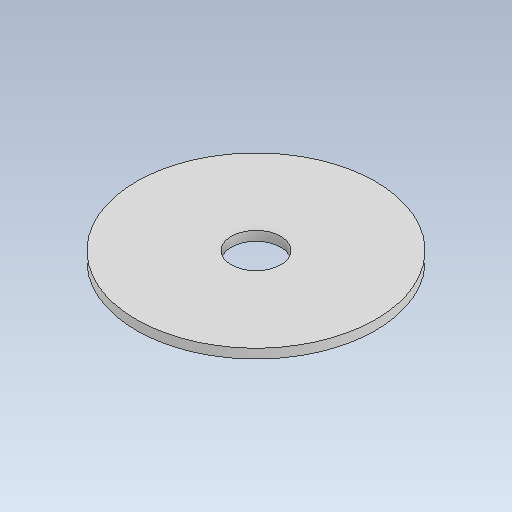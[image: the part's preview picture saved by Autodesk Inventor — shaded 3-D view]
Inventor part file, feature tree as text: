
AUTODESK INVENTOR PART (.ipt)
format: ipt  version: 2023 (Build 270158000, 158)  size: 88,576 bytes
history: native  units: in
note: dims shown in document units (in); Inventor stores cm internally (conversion verified against a paired STEP export)
features: extrude x1, sketch x1
ambient origin geometry x8: Origin, YZ Plane, XZ Plane, XY Plane, X Axis, Y Axis, Z Axis, Center Point
bodies: Solid1 (feature_tree)
feature tree (2):
  extrude  "Extrusion1"  Depth=0.0394in
  sketch  "Sketch1"  dims[d0=0.9984in d1=0.2067in d2=0.0394in d3=0.0in]
